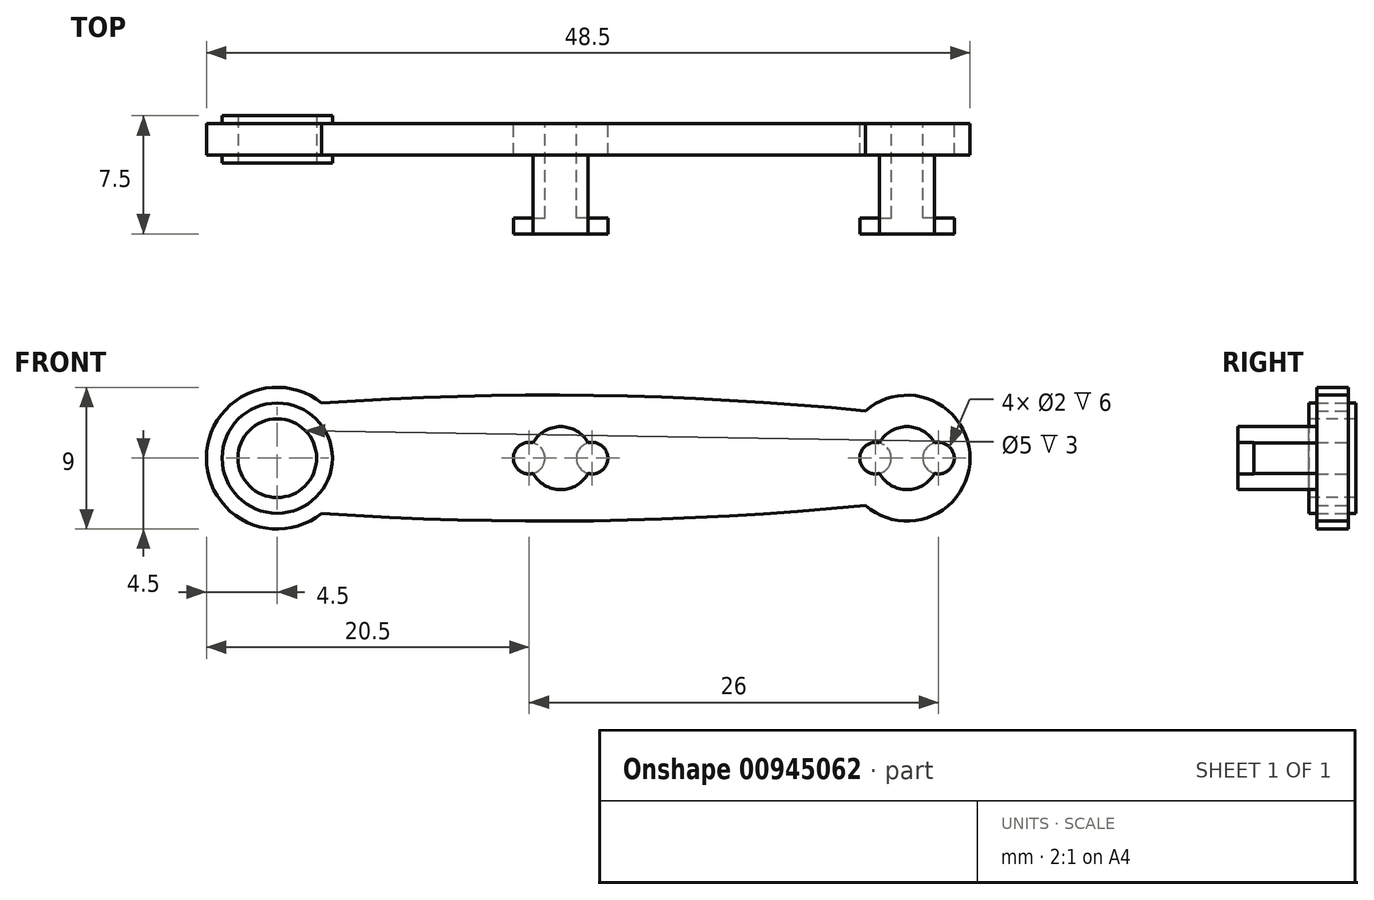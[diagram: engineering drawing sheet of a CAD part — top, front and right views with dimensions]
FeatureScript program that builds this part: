
annotation { "Feature Type Name" : "Feature", "Feature Type Description" : "" }
export const myFeature = defineFeature(function(context is Context, id is Id, definition is map)
    precondition{}
    {
        {
            var Q0;
            Q0=qCreatedBy(makeId("Front.planeOp"),FACE);
            var sketch = newSketch(context, id + "F0", { "sketchPlane" : qUnion([Q0])});
            skArc(sketch, "E0", {"start": v(2.83, 3.5) * mm, "mid": v(-4.5, 0) * mm, "end": v(2.83, -3.5) * mm});
            skArc(sketch, "E1", {"start": v(37.35, -3) * mm, "mid": v(44, 0) * mm, "end": v(37.35, 3) * mm});
            skArc(sketch, "E2", {"start": v(37.35, 3) * mm, "mid": v(20.1, 3.98) * mm, "end": v(2.83, 3.5) * mm});
            skArc(sketch, "E3", {"start": v(2.83, -3.5) * mm, "mid": v(20.1, -3.98) * mm, "end": v(37.35, -3) * mm});
            skSolve(sketch);
        }
        {
            var Q0;
            Q0=makeQuery(id+"F0.imprint","IMPRINT",FACE,{"disambiguationData":[TD([[makeQuery(id+"F0.imprint","IMPRINT",EDGE,{"derivedFrom":sQuery(id+"F0.wireOp",EDGE,"E0")}),1.0]])]});
            extrude(context, id + "F1", {"entities" : qUnion([Q0]), "depth" : 2 * mm, "offsetDistance" : 25 * mm, "symmetric" : true});
        }
        {
            var Q0;
            Q0=qCreatedBy(makeId("Front.planeOp"),FACE);
            var sketch = newSketch(context, id + "F2", { "sketchPlane" : qUnion([Q0])});
            skCircle(sketch, "E4", {"center": v(0, 0) * mm, "radius": 3.5 * mm});
            skSolve(sketch);
        }
        {
            var Q0;
            Q0=makeQuery(id+"F2.imprint","IMPRINT",FACE,{"disambiguationData":[TD([[makeQuery(id+"F2.imprint","IMPRINT",EDGE,{"derivedFrom":sQuery(id+"F2.wireOp",EDGE,"E4")}),1.0]])]});
            extrude(context, id + "F3", {"entities" : qUnion([Q0]), "operationType" : NewBodyOperationType.ADD, "depth" : 3 * mm, "offsetDistance" : 25 * mm, "symmetric" : true});
        }
        {
            var Q0;
            Q0=makeQuery(id+"F3.opExtrude","CAP_FACE",FACE,{"disambiguationData":[OSD([sQuery(id+"F2.wireOp",EDGE,"E4")])],"isStart":false});
            var sketch = newSketch(context, id + "F4", { "sketchPlane" : qUnion([Q0])});
            skCircle(sketch, "E5", {"center": v(0, 0) * mm, "radius": 2.5 * mm});
            skSolve(sketch);
        }
        {
            var Q0;
            Q0=makeQuery(id+"F4.imprint","IMPRINT",FACE,{"disambiguationData":[TD([[makeQuery(id+"F4.imprint","IMPRINT",EDGE,{"derivedFrom":sQuery(id+"F4.wireOp",EDGE,"E5")}),1.0]])]});
            extrude(context, id + "F5", {"entities" : qUnion([Q0]), "operationType" : NewBodyOperationType.REMOVE, "endBound" : BoundingType.THROUGH_ALL, "oppositeDirection" : true, "depth" : 25 * mm, "offsetDistance" : 25 * mm});
        }
        {
            var Q0;
            Q0=makeQuery(id+"F1.opExtrude","CAP_FACE",FACE,{"disambiguationData":[OSD([sQuery(id+"F0.wireOp",EDGE,"E0"),sQuery(id+"F0.wireOp",EDGE,"E1"),sQuery(id+"F0.wireOp",EDGE,"E2"),sQuery(id+"F0.wireOp",EDGE,"E3")])],"isStart":false});
            var sketch = newSketch(context, id + "F6", { "sketchPlane" : qUnion([Q0])});
            skCircle(sketch, "E6", {"center": v(40, 0) * mm, "radius": 2 * mm});
            skCircle(sketch, "E7", {"center": v(18, 0) * mm, "radius": 2 * mm});
            skSolve(sketch);
        }
        {
            var Q0;
            Q0=makeQuery(id+"F6.imprint","IMPRINT",FACE,{"disambiguationData":[TD([[makeQuery(id+"F6.imprint","IMPRINT",EDGE,{"derivedFrom":sQuery(id+"F6.wireOp",EDGE,"E7")}),1.0]])]});
            var Q1;
            Q1=makeQuery(id+"F6.imprint","IMPRINT",FACE,{"disambiguationData":[TD([[makeQuery(id+"F6.imprint","IMPRINT",EDGE,{"derivedFrom":sQuery(id+"F6.wireOp",EDGE,"E6")}),1.0]])]});
            extrude(context, id + "F7", {"entities" : qUnion([Q0, Q1]), "operationType" : NewBodyOperationType.ADD, "depth" : 5 * mm, "offsetDistance" : 25 * mm});
        }
        {
            var Q0;
            Q0=makeQuery(id+"F7.opExtrude","CAP_FACE",FACE,{"disambiguationData":[OSD([sQuery(id+"F6.wireOp",EDGE,"E7")])],"isStart":false});
            var sketch = newSketch(context, id + "F8", { "sketchPlane" : qUnion([Q0])});
            skArc(sketch, "E8", {"start": v(19.75, 0.97) * mm, "mid": v(18, 2) * mm, "end": v(16.25, 0.97) * mm});
            skArc(sketch, "E9", {"start": v(16.25, 0.97) * mm, "mid": v(15, 0) * mm, "end": v(16.25, -0.97) * mm});
            skArc(sketch, "E10", {"start": v(19.75, -0.97) * mm, "mid": v(21, 0) * mm, "end": v(19.75, 0.97) * mm});
            skArc(sketch, "E11.trimOffspring", {"start": v(16.25, -0.97) * mm, "mid": v(18, -2) * mm, "end": v(19.75, -0.97) * mm});
            skArc(sketch, "E12", {"start": v(41.75, 0.97) * mm, "mid": v(40, 2) * mm, "end": v(38.25, 0.97) * mm});
            skArc(sketch, "E13", {"start": v(38.25, 0.97) * mm, "mid": v(37, 0) * mm, "end": v(38.25, -0.97) * mm});
            skArc(sketch, "E14", {"start": v(41.75, -0.97) * mm, "mid": v(43, 0) * mm, "end": v(41.75, 0.97) * mm});
            skArc(sketch, "E15.trimOffspring", {"start": v(38.25, -0.97) * mm, "mid": v(40, -2) * mm, "end": v(41.75, -0.97) * mm});
            skSolve(sketch);
        }
        {
            var Q0;
            {var subQ0=sQuery(id+"F8.wireOp",EDGE,"E9");Q0=makeQuery(id+"F8.imprint","IMPRINT",FACE,{"disambiguationData":[TD([[makeQuery(id+"F8.imprint","IMPRINT",EDGE,{"derivedFrom":subQ0}),1.0]])]});}
            var Q1;
            {var subQ0=sQuery(id+"F8.wireOp",EDGE,"E10");Q1=makeQuery(id+"F8.imprint","IMPRINT",FACE,{"disambiguationData":[TD([[makeQuery(id+"F8.imprint","IMPRINT",EDGE,{"derivedFrom":subQ0}),1.0]])]});}
            var Q2;
            Q2=makeQuery(id+"F8.imprint","IMPRINT",FACE,{"disambiguationData":[TD([[makeQuery(id+"F8.imprint","IMPRINT",EDGE,{"derivedFrom":sQuery(id+"F8.wireOp",EDGE,"E12")}),1.0]])]});
            var Q3;
            {var subQ0=sQuery(id+"F8.wireOp",EDGE,"E8");Q3=makeQuery(id+"F8.imprint","IMPRINT",FACE,{"disambiguationData":[TD([[makeQuery(id+"F8.imprint","IMPRINT",EDGE,{"derivedFrom":subQ0}),1.0]])]});}
            extrude(context, id + "F9", {"entities" : qUnion([Q0, Q1, Q2, Q3]), "operationType" : NewBodyOperationType.ADD, "oppositeDirection" : true, "depth" : 1 * mm, "offsetDistance" : 25 * mm});
        }
        {
            var Q0;
            Q0=makeQuery(id+"F1.opExtrude","CAP_FACE",FACE,{"disambiguationData":[OSD([sQuery(id+"F0.wireOp",EDGE,"E0"),sQuery(id+"F0.wireOp",EDGE,"E1"),sQuery(id+"F0.wireOp",EDGE,"E2"),sQuery(id+"F0.wireOp",EDGE,"E3")])],"isStart":true});
            var sketch = newSketch(context, id + "F10", { "sketchPlane" : qUnion([Q0])});
            skCircle(sketch, "E16", {"center": v(-42, 0) * mm, "radius": 1 * mm});
            skCircle(sketch, "E17", {"center": v(-38, 0) * mm, "radius": 1 * mm});
            skCircle(sketch, "E18", {"center": v(-20, 0) * mm, "radius": 1 * mm});
            skCircle(sketch, "E19", {"center": v(-16, 0) * mm, "radius": 1 * mm});
            skSolve(sketch);
        }
        {
            var Q0;
            Q0=makeQuery(id+"F10.imprint","IMPRINT",FACE,{"disambiguationData":[TD([[makeQuery(id+"F10.imprint","IMPRINT",EDGE,{"derivedFrom":sQuery(id+"F10.wireOp",EDGE,"E16")}),1.0]])]});
            var Q1;
            Q1=makeQuery(id+"F10.imprint","IMPRINT",FACE,{"disambiguationData":[TD([[makeQuery(id+"F10.imprint","IMPRINT",EDGE,{"derivedFrom":sQuery(id+"F10.wireOp",EDGE,"E17")}),1.0]])]});
            var Q2;
            Q2=makeQuery(id+"F10.imprint","IMPRINT",FACE,{"disambiguationData":[TD([[makeQuery(id+"F10.imprint","IMPRINT",EDGE,{"derivedFrom":sQuery(id+"F10.wireOp",EDGE,"E18")}),1.0]])]});
            var Q3;
            Q3=makeQuery(id+"F10.imprint","IMPRINT",FACE,{"disambiguationData":[TD([[makeQuery(id+"F10.imprint","IMPRINT",EDGE,{"derivedFrom":sQuery(id+"F10.wireOp",EDGE,"E19")}),1.0]])]});
            var Q4;
            {var subQ0=sQuery(id+"F8.wireOp",EDGE,"E14");Q4=makeQuery(id+"F9.boolean.opBoolean","SPLIT",FACE,{"disambiguationData":[TD([makeQuery(id+"F9.opExtrude","SWEPT_FACE",FACE,{"disambiguationData":[OSD([subQ0])]})])],"derivedFrom":makeQuery(id+"F9.opExtrude","CAP_FACE",FACE,{"disambiguationData":[OSD([sQuery(id+"F8.wireOp",EDGE,"E12"),sQuery(id+"F8.wireOp",EDGE,"E13"),subQ0,sQuery(id+"F8.wireOp",EDGE,"E15.trimOffspring")])],"isStart":false})});}
            extrude(context, id + "F11", {"entities" : qUnion([Q0, Q1, Q2, Q3]), "operationType" : NewBodyOperationType.REMOVE, "endBound" : BoundingType.UP_TO_SURFACE, "oppositeDirection" : true, "depth" : 25 * mm, "endBoundEntityFace" : qUnion([Q4]), "offsetDistance" : 25 * mm});
        }
    });
